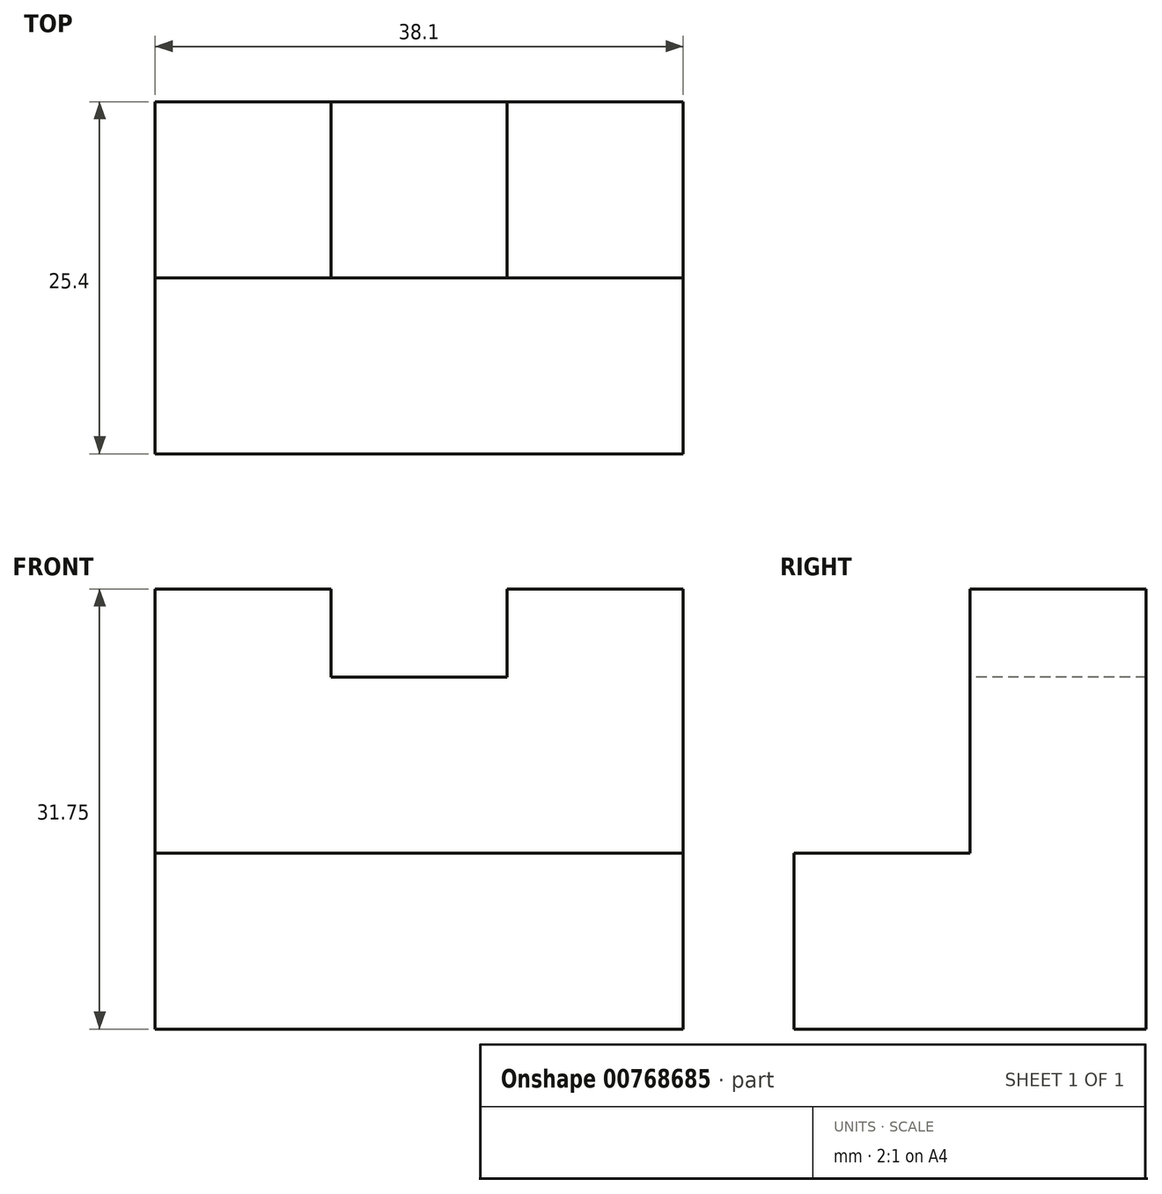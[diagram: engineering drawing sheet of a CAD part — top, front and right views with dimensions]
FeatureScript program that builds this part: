
annotation { "Feature Type Name" : "Feature", "Feature Type Description" : "" }
export const myFeature = defineFeature(function(context is Context, id is Id, definition is map)
    precondition{}
    {
        {
            var Q0;
            Q0=qCreatedBy(makeId("Right.planeOp"),FACE);
            var sketch = newSketch(context, id + "F0", { "sketchPlane" : qUnion([Q0])});
            skLineSegment(sketch, "E0", {"start": v(0, 0) * mm, "end": v(25.4, 0) * mm});
            skLineSegment(sketch, "E1", {"start": v(25.4, 0) * mm, "end": v(25.4, 31.75) * mm});
            skLineSegment(sketch, "E2", {"start": v(25.4, 31.75) * mm, "end": v(12.7, 31.75) * mm});
            skLineSegment(sketch, "E3", {"start": v(12.7, 31.75) * mm, "end": v(12.7, 12.7) * mm});
            skLineSegment(sketch, "E4", {"start": v(12.7, 12.7) * mm, "end": v(0, 12.7) * mm});
            skLineSegment(sketch, "E5", {"start": v(0, 12.7) * mm, "end": v(0, 0) * mm});
            skSolve(sketch);
        }
        {
            var Q0;
            Q0 = qSketchRegion(id + "F0", true);
            extrude(context, id + "F1", {"entities" : qUnion([Q0]), "depth" : 38.1 * mm, "offsetDistance" : 25.4 * mm});
        }
        {
            var Q0;
            Q0=makeQuery(id+"F1.opExtrude","SWEPT_FACE",FACE,{"disambiguationData":[OSD([sQuery(id+"F0.wireOp",EDGE,"E3")])]});
            var sketch = newSketch(context, id + "F2", { "sketchPlane" : qUnion([Q0])});
            skLineSegment(sketch, "E6", {"start": v(0, 31.75) * mm, "end": v(12.7, 31.75) * mm});
            skLineSegment(sketch, "E7", {"start": v(12.7, 31.75) * mm, "end": v(12.7, 25.4) * mm});
            skLineSegment(sketch, "E8", {"start": v(12.7, 25.4) * mm, "end": v(25.4, 25.4) * mm});
            skLineSegment(sketch, "E9", {"start": v(25.4, 25.4) * mm, "end": v(25.4, 31.75) * mm});
            skSolve(sketch);
        }
        {
            var Q0;
            {var subQ0=sQuery(id+"F2.wireOp",EDGE,"E7");Q0=makeQuery(id+"F2.imprint","IMPRINT",FACE,{"disambiguationData":[TD([[makeQuery(id+"F2.imprint","IMPRINT",EDGE,{"derivedFrom":subQ0}),1.0]])]});}
            extrude(context, id + "F3", {"entities" : qUnion([Q0]), "operationType" : NewBodyOperationType.REMOVE, "endBound" : BoundingType.UP_TO_NEXT, "oppositeDirection" : true, "depth" : 25.4 * mm, "offsetDistance" : 25.4 * mm});
        }
    });
